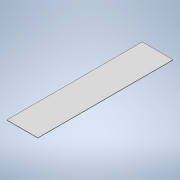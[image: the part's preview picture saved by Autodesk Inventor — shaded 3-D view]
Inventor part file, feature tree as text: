
AUTODESK INVENTOR PART (.ipt)
format: ipt  version: 2020 (Build 240168000, 168)  size: 91,136 bytes
history: native  units: in
note: dims shown in document units (in); Inventor stores cm internally (conversion verified against a paired STEP export)
features: extrude x1, sketch x1
ambient origin geometry x8: Origin, YZ Plane, XZ Plane, XY Plane, X Axis, Y Axis, Z Axis, Center Point
bodies: Solid1 (feature_tree)
feature tree (2):
  extrude  "Extrusion1"  Depth=17.5in
  sketch  "Sketch1"  dims[d0=4.0in d1=17.5in d2=0.04in d3=0.0in]
